# Revit family: Workstation-Teknion-Expansion_Desking_Enclosed_06-R2012
name_source: partatom
category: Furniture Systems
revit_build: Autodesk Revit Architecture 2013 (Build: 20130531_2115(x64)
units: mm (PartAtom-declared; Revit-internal decimal feet)

## types (1)
- 66" x 72"
    Assembly Code = E2020200
    Depth = 132"
    Description = 5'-6" x 6' workstation
    Height = 41 13/16"
    Manufacturer = Teknion
    Manufacturer Fax = 416.661.4586
    Model = Expansion Desking - Enclosed 06
    Product Line = Expansion Desking
Expansion Desking
Expansion Desking
    Product Page URL = http://teknionplanningtool.com
    Storage Unit Trim Finish = Source Laminate - Teknion - DE - Latte
    Sustainability Data = http://www.teknion.com
    URL = http://www.teknion.com
    Unit Weight URL = http://www.teknion.com
    Warranty = http://www.teknion.com
    Width = 338"

## geometry (parser evidence)
native form markers: Blend x68, Sweep x27
no freeform markers — native parametric forms only
